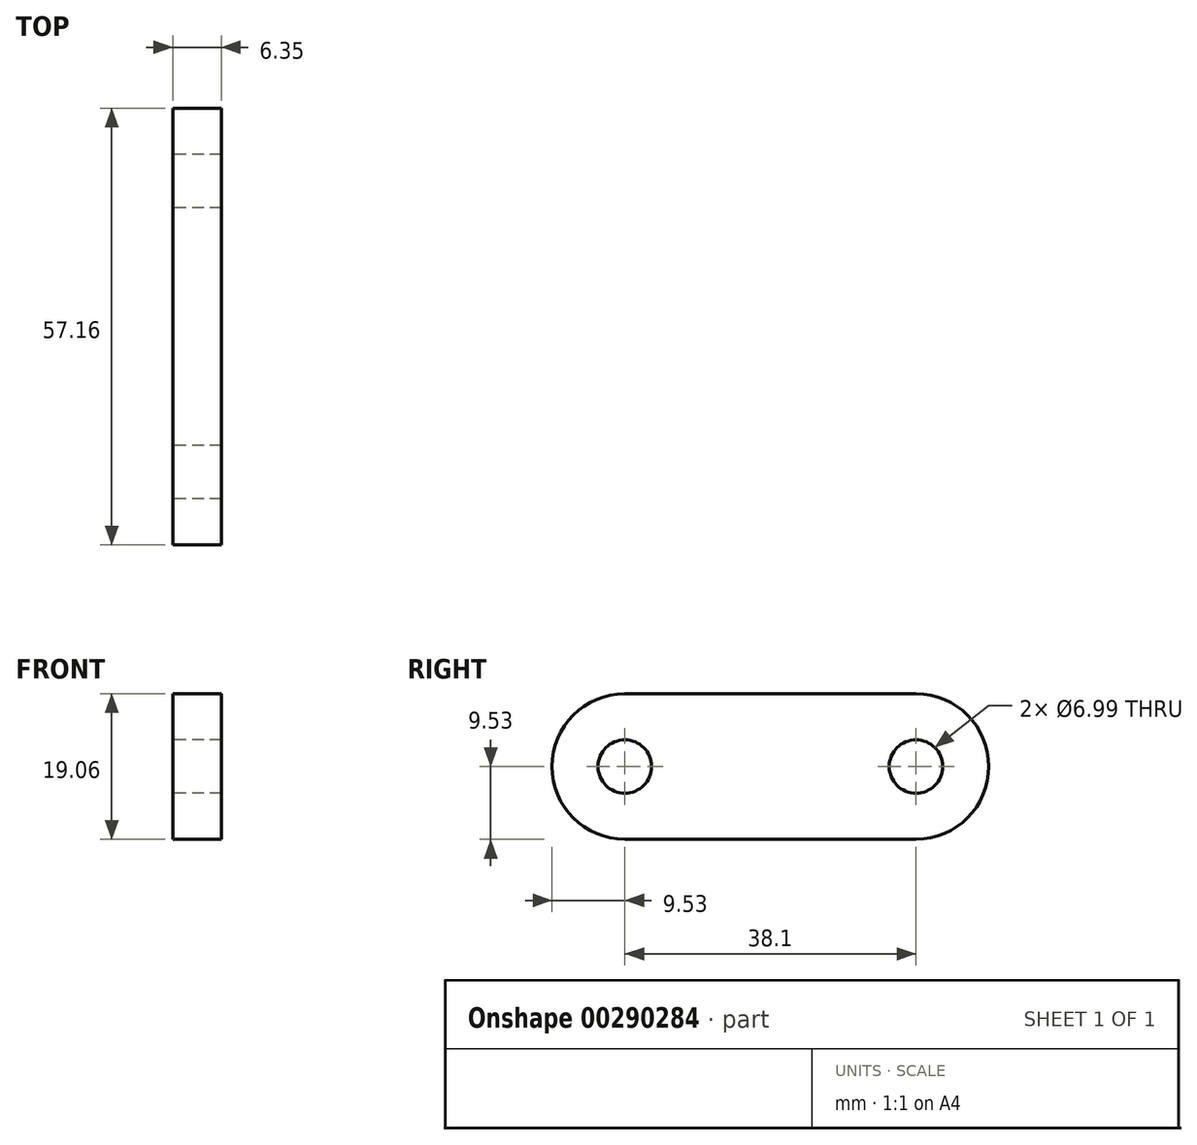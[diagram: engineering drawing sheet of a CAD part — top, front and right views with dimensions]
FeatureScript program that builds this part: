
annotation { "Feature Type Name" : "Feature", "Feature Type Description" : "" }
export const myFeature = defineFeature(function(context is Context, id is Id, definition is map)
    precondition{}
    {
        {
            var Q0;
            Q0=qCreatedBy(makeId("Right.planeOp"),FACE);
            var sketch = newSketch(context, id + "F0", { "sketchPlane" : qUnion([Q0])});
            skLineSegment(sketch, "E0.bottom", {"start": v(19.05, -9.52) * mm, "end": v(-19.05, -9.53) * mm});
            skLineSegment(sketch, "E0.top", {"start": v(19.05, 9.53) * mm, "end": v(-19.05, 9.53) * mm});
            skLineSegment(sketch, "E0.left", {"start": v(19.05, -9.52) * mm, "end": v(19.05, 9.53) * mm});
            skLineSegment(sketch, "E0.right", {"start": v(-19.05, -9.53) * mm, "end": v(-19.05, 9.53) * mm});
            skPoint(sketch, "E0.middle", {"position": v(0, 0) * mm});
            skArc(sketch, "E1", {"start": v(19.05, -9.53) * mm, "mid": v(28.58, 0) * mm, "end": v(19.05, 9.53) * mm});
            skArc(sketch, "E2", {"start": v(-19.05, 9.53) * mm, "mid": v(-28.57, 0) * mm, "end": v(-19.05, -9.53) * mm});
            skCircle(sketch, "E3", {"center": v(-19.05, 0) * mm, "radius": 3.5 * mm});
            skCircle(sketch, "E4", {"center": v(19.05, 0) * mm, "radius": 3.5 * mm});
            skSolve(sketch);
        }
        {
            var Q0;
            Q0 = qSketchRegion(id + "F0", true);
            extrude(context, id + "F1", {"entities" : qUnion([Q0]), "depth" : 6.35 * mm});
        }
    });
